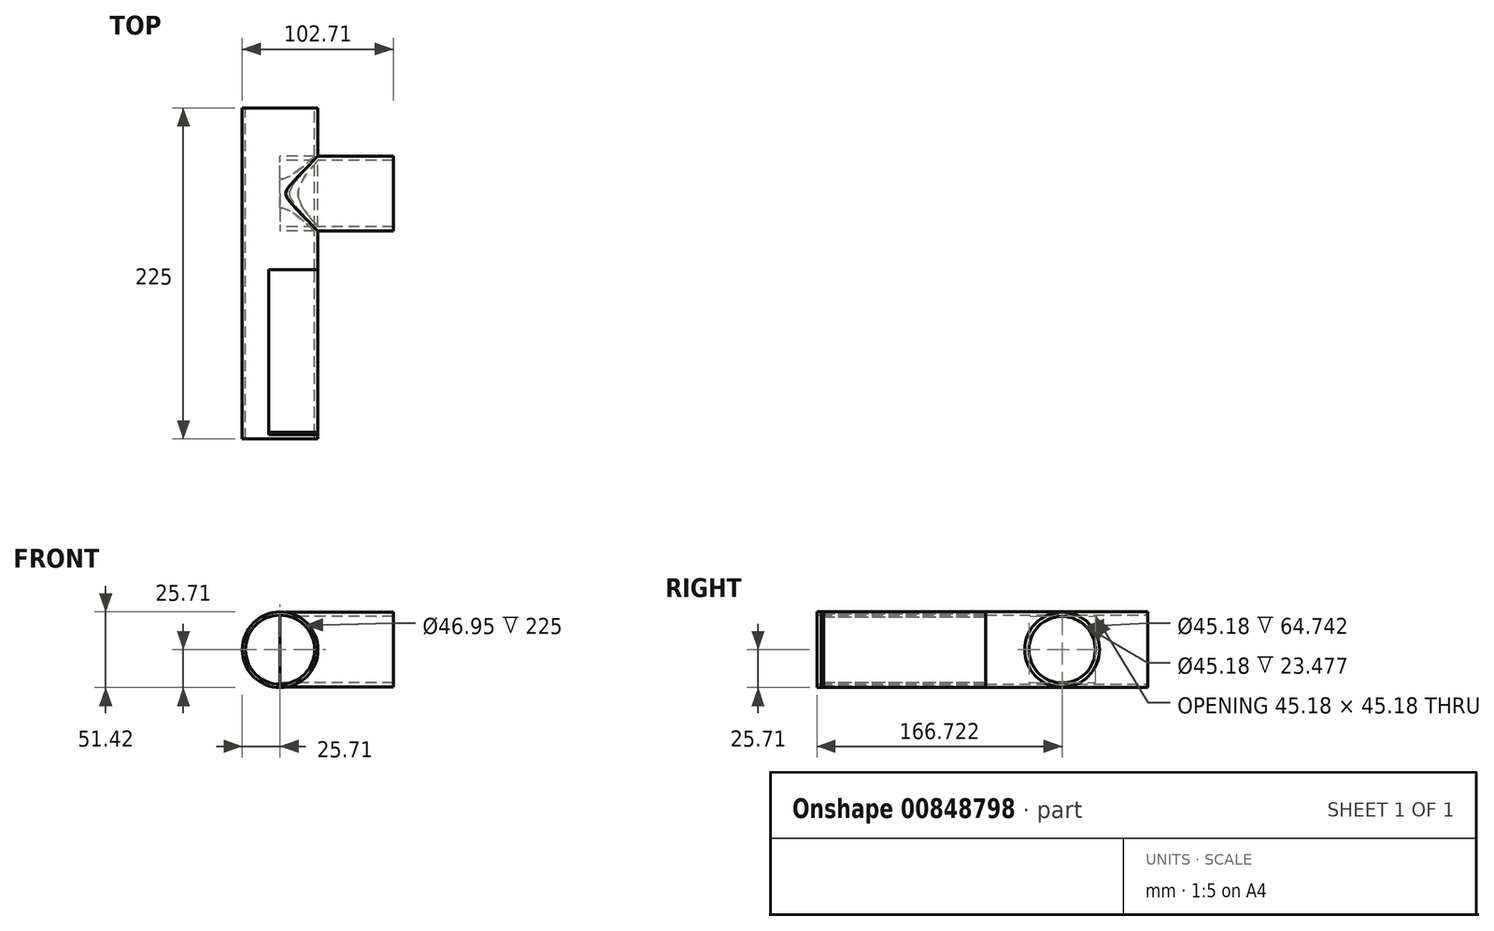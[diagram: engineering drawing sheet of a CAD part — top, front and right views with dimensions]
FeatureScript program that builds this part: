
annotation { "Feature Type Name" : "Feature", "Feature Type Description" : "" }
export const myFeature = defineFeature(function(context is Context, id is Id, definition is map)
    precondition{}
    {
        {
            var Q0;
            Q0=qCreatedBy(makeId("Front.planeOp"),FACE);
            var sketch = newSketch(context, id + "F0", { "sketchPlane" : qUnion([Q0])});
            skCircle(sketch, "E0", {"center": v(0, 0) * mm, "radius": 25.7 * mm});
            skCircle(sketch, "E1", {"center": v(0, 0) * mm, "radius": 23.47 * mm});
            skSolve(sketch);
        }
        {
            var Q0;
            Q0 = qSketchRegion(id + "F0", true);
            extrude(context, id + "F1", {"entities" : qUnion([Q0]), "depth" : 114 * mm, "offsetDistance" : 25 * mm});
        }
        {
            var Q0;
            Q0=qCreatedBy(makeId("Right.planeOp"),FACE);
            var sketch = newSketch(context, id + "F2", { "sketchPlane" : qUnion([Q0])});
            skCircle(sketch, "E2", {"center": v(-58.28, 0) * mm, "radius": 25.43 * mm});
            skCircle(sketch, "E3", {"center": v(-58.28, 0) * mm, "radius": 22.6 * mm});
            skSolve(sketch);
        }
        {
            var Q0;
            Q0 = qSketchRegion(id + "F2", true);
            extrude(context, id + "F3", {"entities" : qUnion([Q0]), "operationType" : NewBodyOperationType.ADD, "depth" : 77 * mm, "offsetDistance" : 25 * mm});
        }
        {
            var Q0;
            Q0=makeQuery(id+"F1.opExtrude","CAP_FACE",FACE,{"disambiguationData":[OSD([sQuery(id+"F0.wireOp",EDGE,"E0"),sQuery(id+"F0.wireOp",EDGE,"E1")])],"isStart":false});
            extrude(context, id + "F4", {"entities" : qUnion([Q0]), "operationType" : NewBodyOperationType.ADD, "depth" : 111 * mm, "offsetDistance" : 25 * mm});
        }
        {
            var Q0;
            Q0=qCreatedBy(makeId("Top.planeOp"),FACE);
            var sketch = newSketch(context, id + "F5", { "sketchPlane" : qUnion([Q0])});
            skLineSegment(sketch, "E4.bottom", {"start": v(37.6, -110.13) * mm, "end": v(-7.7, -110.13) * mm});
            skLineSegment(sketch, "E4.top", {"start": v(37.6, -220.42) * mm, "end": v(-7.7, -220.42) * mm});
            skLineSegment(sketch, "E4.left", {"start": v(37.6, -110.13) * mm, "end": v(37.6, -220.42) * mm});
            skLineSegment(sketch, "E4.right", {"start": v(-7.7, -110.13) * mm, "end": v(-7.7, -220.42) * mm});
            skSolve(sketch);
        }
        {
            var Q0;
            Q0 = qSketchRegion(id + "F5", true);
            extrude(context, id + "F6", {"entities" : qUnion([Q0]), "operationType" : NewBodyOperationType.REMOVE, "endBound" : BoundingType.SYMMETRIC, "oppositeDirection" : true, "depth" : 100 * mm, "offsetDistance" : 25 * mm});
        }
        {
            var Q0;
            Q0=makeQuery(id+"F6.boolean.opBoolean","COPY",FACE,{"derivedFrom":makeQuery(id+"F6.opExtrude","SWEPT_FACE",FACE,{"disambiguationData":[OSD([sQuery(id+"F5.wireOp",EDGE,"E4.bottom")])]})});
            extrude(context, id + "F7", {"entities" : qUnion([Q0]), "depth" : 112 * mm, "offsetDistance" : 25 * mm});
        }
    });
